# Revit family: NLRS_52_GM_HWA_rond_MR
name_source: partatom
category: Generic Models
revit_build: Autodesk Revit 2017 (Build: 20190507_1515(x64)
units: mm (PartAtom-declared; Revit-internal decimal feet)

## family parameters
Always vertical = Yes
Can host rebar = No
Cut with Voids When Loaded = No
Part Type = Normal
Room Calculation Point = No
Round Connector Dimension = Use Diameter
Shared = No
Work Plane-Based = No

## types (2) — shared parameters
Description = Hemelwater afvoer
Manufacturer = Meilof Riks bv
NLRS_C_Bochten_72gr = No
NLRS_C_hoek = 40.00°
Type Comments = HWA

## per-type parameters (varying)
| type | Model | NLRS_C_Materiaal | NLRS_C_diameter | NLRS_C_radius | URL | a1 | a2 |
| HWA 80 |  | RAL 9010 | 80 mm  [stored 0.262467 ft] | 120 mm  [stored 0.393701 ft] | https://www.meilofriks.nl | 44 mm | 84 mm  [stored 0.275591 ft] |
| HWA 100 | HWA 100 | RAL 7016 | 100 mm  [stored 0.328084 ft] | 150 mm  [stored 0.492126 ft] |  | 55 mm | 95 mm  [stored 0.31168 ft] |

note: [stored X ft] marks values corroborated as IEEE doubles in the binary element streams (Revit-internal decimal feet)

## geometry (parser evidence)
native form markers: Sweep x12
no freeform markers — native parametric forms only
